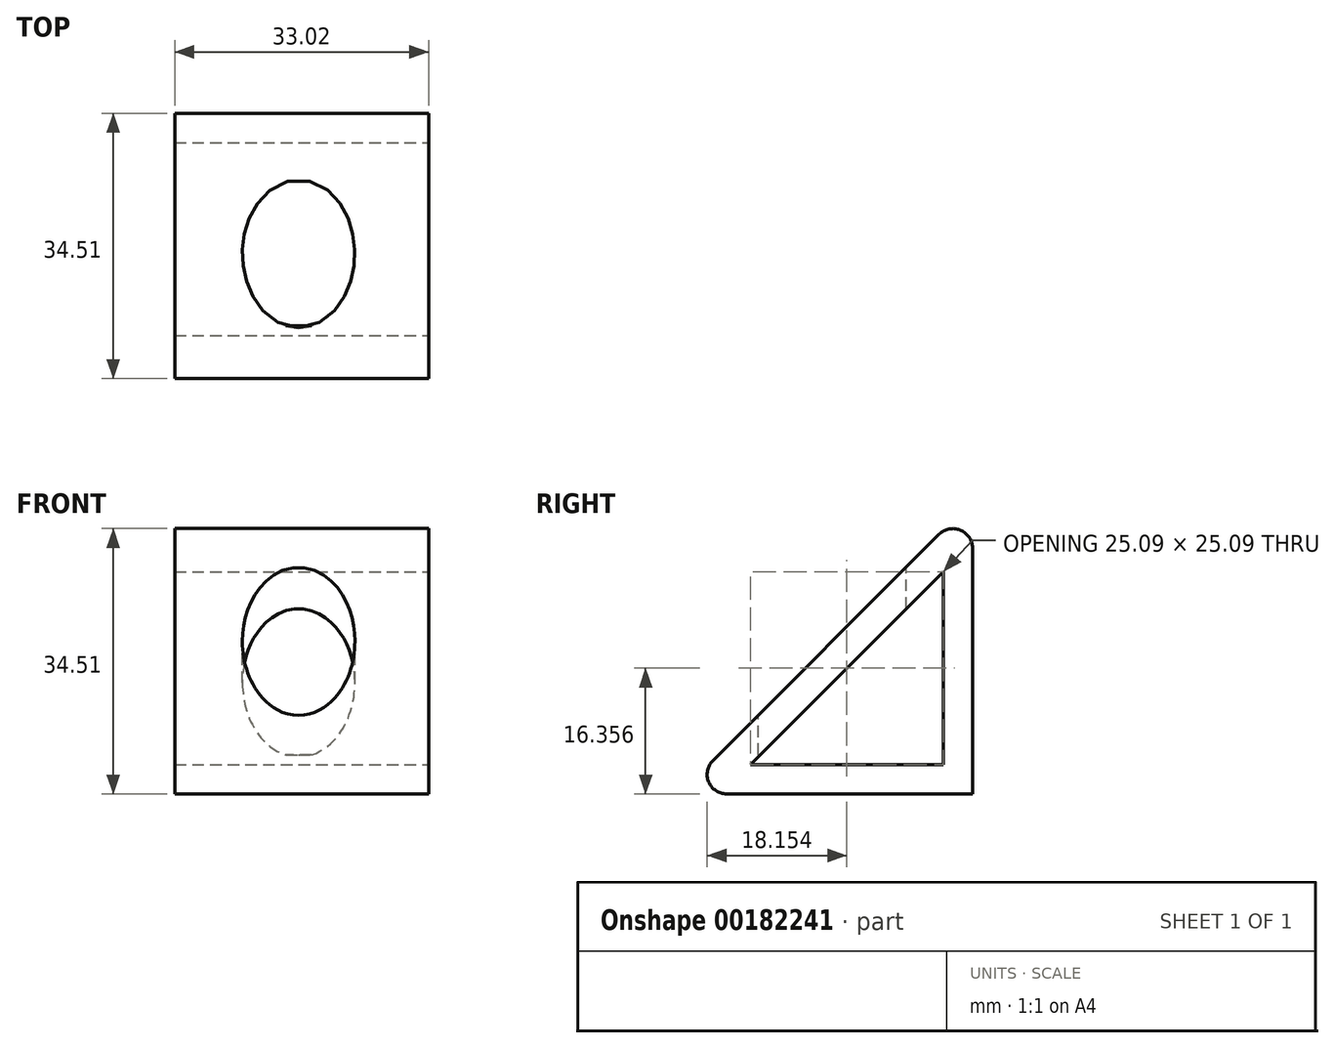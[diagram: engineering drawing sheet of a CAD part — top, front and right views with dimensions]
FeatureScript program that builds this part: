
annotation { "Feature Type Name" : "Feature", "Feature Type Description" : "" }
export const myFeature = defineFeature(function(context is Context, id is Id, definition is map)
    precondition{}
    {
        {
            var Q0;
            Q0=qCreatedBy(makeId("Right.planeOp"),FACE);
            var sketch = newSketch(context, id + "F0", { "sketchPlane" : qUnion([Q0])});
            skLineSegment(sketch, "E0", {"start": v(0, 0) * mm, "end": v(0, 38.1) * mm});
            skLineSegment(sketch, "E1", {"start": v(0, 38.1) * mm, "end": v(-38.1, 0) * mm});
            skLineSegment(sketch, "E2", {"start": v(-38.1, 0) * mm, "end": v(0, 0) * mm});
            skSolve(sketch);
        }
        {
            var Q0;
            Q0=qSketchRegion(id+"F0",true);
            extrude(context, id + "F1", {"entities" : qUnion([Q0]), "depth" : 33.02 * mm});
        }
        {
            var Q0;
            Q0=makeQuery(id+"F1.opExtrude","SWEPT_EDGE",EDGE,{"disambiguationData":[OSD([sQuery(id+"F0.wireOp",EDGE,"E0"),sQuery(id+"F0.wireOp",EDGE,"E1")])]});
            var Q1;
            Q1=makeQuery(id+"F1.opExtrude","SWEPT_EDGE",EDGE,{"disambiguationData":[OSD([sQuery(id+"F0.wireOp",EDGE,"E1"),sQuery(id+"F0.wireOp",EDGE,"E2")])]});
            fillet(context, id + "F2", {"entities" : qUnion([Q0, Q1]), "radius" : 2.54 * mm, "tangentPropagation" : true, "allowEdgeOverflow" : false});
        }
        {
            var Q0;
            Q0=makeQuery(id+"F1.opExtrude","CAP_FACE",FACE,{"disambiguationData":[OSD([sQuery(id+"F0.wireOp",EDGE,"E0"),sQuery(id+"F0.wireOp",EDGE,"E1"),sQuery(id+"F0.wireOp",EDGE,"E2")])],"isStart":false});
            var sketch = newSketch(context, id + "F3", { "sketchPlane" : qUnion([Q0])});
            skLineSegment(sketch, "E3", {"start": v(-3.81, 3.81) * mm, "end": v(-3.81, 28.9) * mm});
            skLineSegment(sketch, "E4", {"start": v(-3.8, 28.9) * mm, "end": v(-28.9, 3.8) * mm});
            skLineSegment(sketch, "E5", {"start": v(-28.9, 3.81) * mm, "end": v(-3.8, 3.81) * mm});
            skSolve(sketch);
        }
        {
            var Q0;
            Q0=qSketchRegion(id+"F3",true);
            extrude(context, id + "F4", {"entities" : qUnion([Q0]), "operationType" : NewBodyOperationType.REMOVE, "endBound" : BoundingType.THROUGH_ALL, "oppositeDirection" : true, "depth" : 25.4 * mm});
        }
        {
            var Q0;
            Q0=qCreatedBy(makeId("Top.planeOp"),FACE);
            cPlane(context, id + "F5", {"entities" : qUnion([Q0]), "cplaneType" : CPlaneType.OFFSET, "offset" : 50.8 * mm, "width" : 152.4 * mm, "height" : 152.4 * mm});
        }
        {
            var Q0;
            Q0=qCreatedBy(id+"F5.planeOp",FACE);
            var sketch = newSketch(context, id + "F6", { "sketchPlane" : qUnion([Q0])});
            skEllipse(sketch, "E6", {"center": v(16.12, -18.26) * mm, "majorRadius": 9.63 * mm, "minorRadius": 7.31 * mm, "majorAxis": v(0, -1)});
            skSolve(sketch);
        }
        {
            var Q0;
            Q0=qSketchRegion(id+"F6",true);
            extrude(context, id + "F7", {"entities" : qUnion([Q0]), "operationType" : NewBodyOperationType.REMOVE, "oppositeDirection" : true, "depth" : 45.72 * mm});
        }
    });
